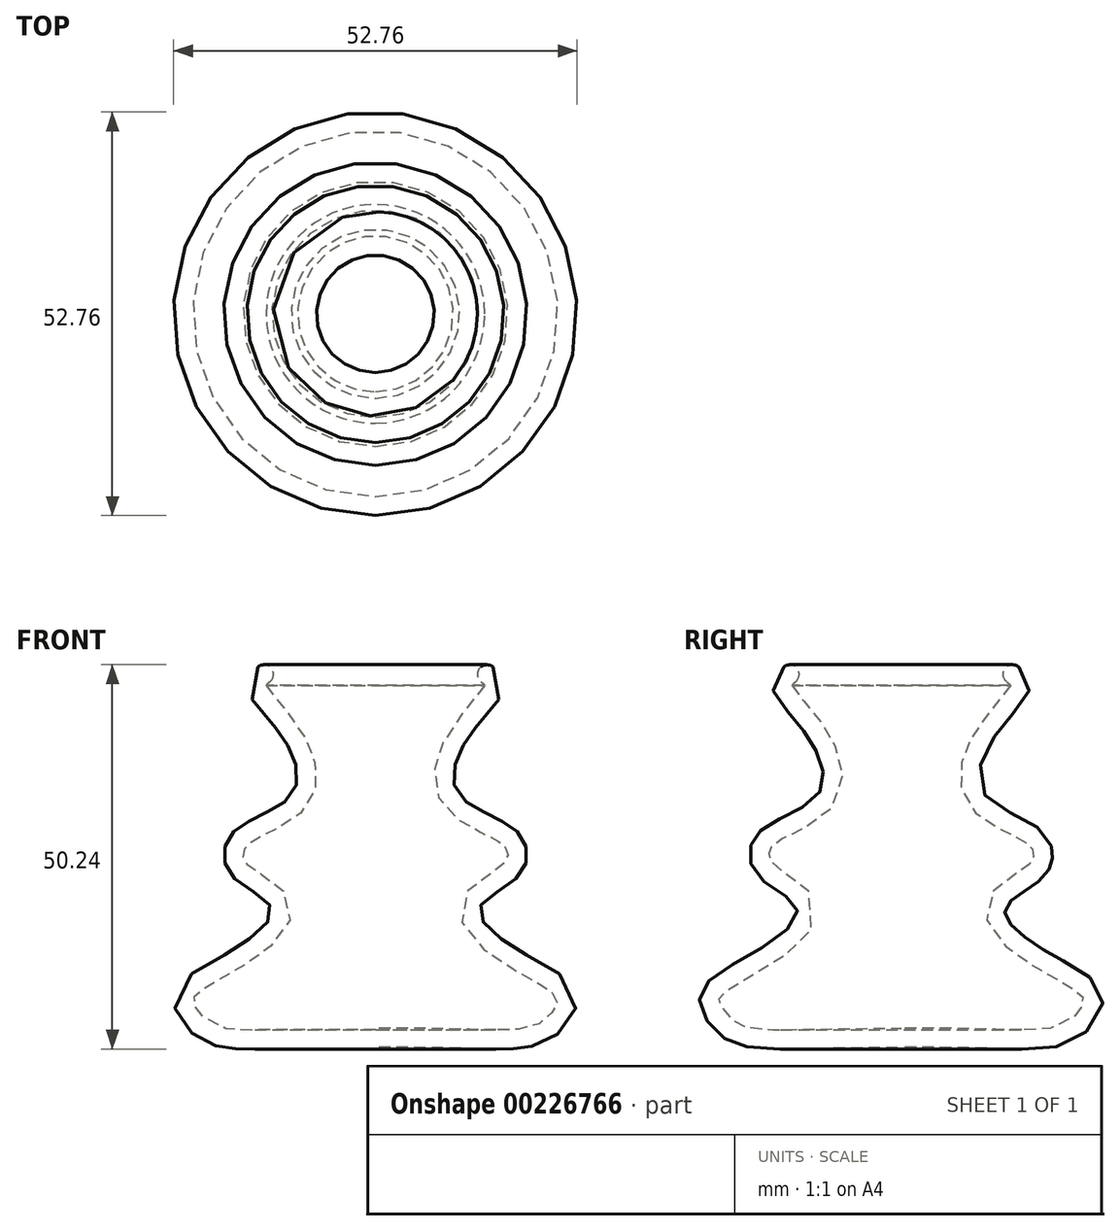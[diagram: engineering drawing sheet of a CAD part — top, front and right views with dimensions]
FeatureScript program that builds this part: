
annotation { "Feature Type Name" : "Feature", "Feature Type Description" : "" }
export const myFeature = defineFeature(function(context is Context, id is Id, definition is map)
    precondition{}
    {
        {
            var Q0;
            Q0=qCreatedBy(makeId("Right.planeOp"),FACE);
            var sketch = newSketch(context, id + "F0", { "sketchPlane" : qUnion([Q0])});
            skLineSegment(sketch, "E0", {"start": v(0, 43.07) * mm, "end": v(0, -40.1) * mm, "construction": true});
            skLineSegment(sketch, "E1", {"start": v(0, 27.79) * mm, "end": v(0, -22.21) * mm});
            skLineSegment(sketch, "E2", {"start": v(0, 27.79) * mm, "end": v(-15, 27.79) * mm});
            skFitSpline(sketch, "E3", {"points": [v(-15, 27.79) * mm, v(-14.88, 21.68) * mm, v(-10.93, 16.16) * mm, v(-10.76, 11) * mm, v(-16.8, 7.18) * mm, v(-19.64, 4.16) * mm, v(-18.58, 0) * mm, v(-13.57, -4.14) * mm, v(-19.09, -9.74) * mm, v(-26.3, -15.34) * mm, v(-23.55, -20.72) * mm, v(0, -22.21) * mm], "startDerivative": vector(-117.34, -82.26) * mm, "endDerivative": vector(298, -0.04) * mm});
            skSolve(sketch);
        }
        {
            var Q0;
            Q0=makeQuery(id+"F0.imprint","IMPRINT",FACE,{"disambiguationData":[TD([[makeQuery(id+"F0.imprint","IMPRINT",EDGE,{"derivedFrom":sQuery(id+"F0.wireOp",EDGE,"E2")}),1.0]])]});
            var Q1;
            Q1=sQuery(id+"F0.wireOp",EDGE,"E0");
            revolve(context, id + "F1", {"entities" : qUnion([Q0]), "axis" : qUnion([Q1]), "revolveType" : RevolveType.FULL});
        }
        {
            var Q0;
            Q0=makeQuery(id+"F1.opRevolve","SWEPT_FACE",FACE,{"disambiguationData":[OSD([sQuery(id+"F0.wireOp",EDGE,"E2")])]});
            shell(context, id + "F2", {"entities" : qUnion([Q0]), "thickness" : 2.5 * mm});
        }
        {
            var Q0;
            Q0=makeQuery(id+"F1.opRevolve","SWEPT_FACE",FACE,{"disambiguationData":[OSD([sQuery(id+"F0.wireOp",EDGE,"E2")])]});
            fillet(context, id + "F3", {"entities" : qUnion([Q0]), "radius" : 1.25 * mm, "tangentPropagation" : true, "allowEdgeOverflow" : false});
        }
    });
